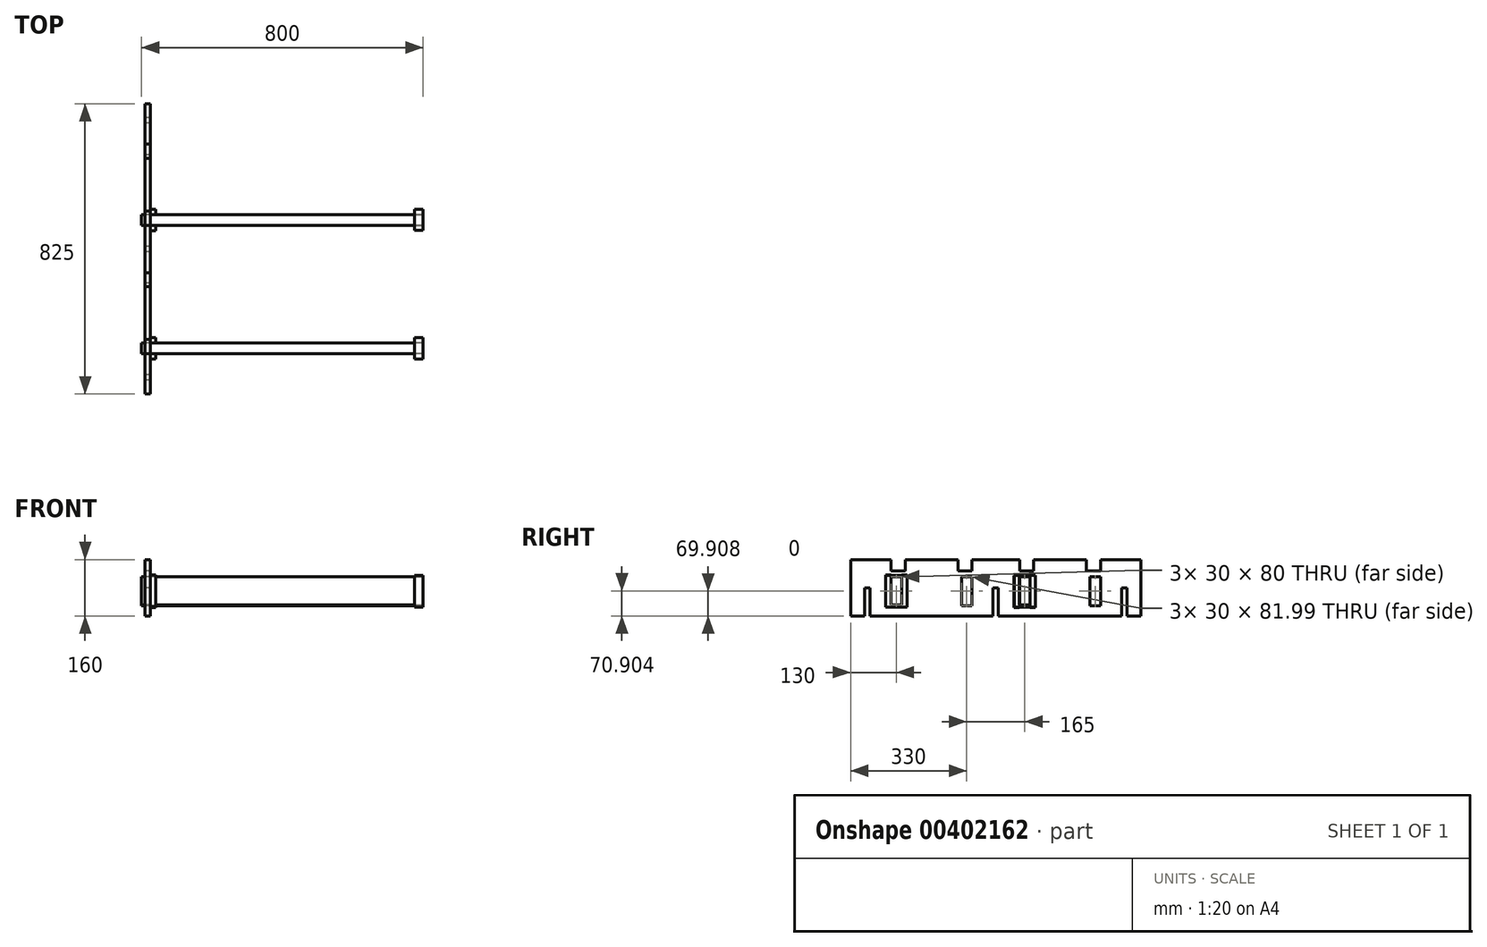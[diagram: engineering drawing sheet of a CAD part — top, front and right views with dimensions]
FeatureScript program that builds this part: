
annotation { "Feature Type Name" : "Feature", "Feature Type Description" : "" }
export const myFeature = defineFeature(function(context is Context, id is Id, definition is map)
    precondition{}
    {
        {
            var Q0;
            Q0=qCreatedBy(makeId("Right.planeOp"),FACE);
            var sketch = newSketch(context, id + "F0", { "sketchPlane" : qUnion([Q0])});
            skLineSegment(sketch, "E0.bottom", {"start": v(-412.5, 80) * mm, "end": v(-297.5, 80) * mm});
            skLineSegment(sketch, "E0.top", {"start": v(-412.5, -80) * mm, "end": v(-372.5, -80) * mm});
            skLineSegment(sketch, "E0.left", {"start": v(-412.5, 80) * mm, "end": v(-412.5, -80) * mm});
            skLineSegment(sketch, "E0.right", {"start": v(412.5, 80) * mm, "end": v(412.5, -80) * mm});
            skLineSegment(sketch, "E1", {"start": v(-372.5, -80) * mm, "end": v(-372.5, 0) * mm});
            skLineSegment(sketch, "E2", {"start": v(-372.5, 0) * mm, "end": v(-357.5, 0) * mm});
            skLineSegment(sketch, "E3", {"start": v(-357.5, 0) * mm, "end": v(-357.5, -80) * mm});
            skLineSegment(sketch, "E4", {"start": v(-7.5, -80) * mm, "end": v(-7.5, 0) * mm});
            skLineSegment(sketch, "E5", {"start": v(-7.5, 0) * mm, "end": v(7.5, 0) * mm});
            skLineSegment(sketch, "E6", {"start": v(7.5, 0) * mm, "end": v(7.5, -80) * mm});
            skLineSegment(sketch, "E7", {"start": v(357.5, -80) * mm, "end": v(357.5, 0) * mm});
            skLineSegment(sketch, "E8", {"start": v(357.5, 0) * mm, "end": v(372.5, 0) * mm});
            skLineSegment(sketch, "E9", {"start": v(372.5, 0) * mm, "end": v(372.5, -80) * mm});
            skLineSegment(sketch, "E10.trimOffspring", {"start": v(372.5, -80) * mm, "end": v(412.5, -80) * mm});
            skLineSegment(sketch, "E11", {"start": v(-357.5, -80) * mm, "end": v(-7.5, -80) * mm});
            skLineSegment(sketch, "E12", {"start": v(7.5, -80) * mm, "end": v(357.5, -80) * mm});
            skLineSegment(sketch, "E13", {"start": v(-297.5, 80) * mm, "end": v(-297.5, 48) * mm});
            skLineSegment(sketch, "E14", {"start": v(-297.5, 48) * mm, "end": v(-257.5, 48) * mm});
            skLineSegment(sketch, "E15", {"start": v(-257.5, 48) * mm, "end": v(-257.5, 80) * mm});
            skLineSegment(sketch, "E16", {"start": v(-257.5, 80) * mm, "end": v(-107.5, 80) * mm});
            skLineSegment(sketch, "E17", {"start": v(-107.5, 80) * mm, "end": v(-107.5, 48) * mm});
            skLineSegment(sketch, "E18", {"start": v(-107.5, 48) * mm, "end": v(-67.5, 48) * mm});
            skLineSegment(sketch, "E19", {"start": v(-67.5, 48) * mm, "end": v(-67.5, 80) * mm});
            skLineSegment(sketch, "E20", {"start": v(-67.5, 80) * mm, "end": v(67.5, 80) * mm});
            skLineSegment(sketch, "E21", {"start": v(67.5, 80) * mm, "end": v(67.5, 48) * mm});
            skLineSegment(sketch, "E22", {"start": v(67.5, 48) * mm, "end": v(107.5, 48) * mm});
            skLineSegment(sketch, "E23", {"start": v(107.5, 48) * mm, "end": v(107.5, 80) * mm});
            skLineSegment(sketch, "E24", {"start": v(107.5, 80) * mm, "end": v(257.5, 80) * mm});
            skLineSegment(sketch, "E25", {"start": v(257.5, 80) * mm, "end": v(257.5, 48) * mm});
            skLineSegment(sketch, "E26", {"start": v(257.5, 48) * mm, "end": v(297.5, 48) * mm});
            skLineSegment(sketch, "E27", {"start": v(297.5, 48) * mm, "end": v(297.5, 80) * mm});
            skLineSegment(sketch, "E28.trimOffspring", {"start": v(297.5, 80) * mm, "end": v(412.5, 80) * mm});
            skLineSegment(sketch, "E29.bottom", {"start": v(-297.5, 30.9) * mm, "end": v(-267.5, 30.9) * mm});
            skLineSegment(sketch, "E29.top", {"start": v(-297.5, -49.1) * mm, "end": v(-267.5, -49.1) * mm});
            skLineSegment(sketch, "E29.left", {"start": v(-297.5, 30.9) * mm, "end": v(-297.5, -49.1) * mm});
            skLineSegment(sketch, "E29.right", {"start": v(-267.5, 30.9) * mm, "end": v(-267.5, -49.1) * mm});
            skLineSegment(sketch, "E30.bottom", {"start": v(-67.5, 30.9) * mm, "end": v(-97.5, 30.9) * mm});
            skLineSegment(sketch, "E30.top", {"start": v(-67.5, -51.09) * mm, "end": v(-97.5, -51.09) * mm});
            skLineSegment(sketch, "E30.left", {"start": v(-67.5, 30.9) * mm, "end": v(-67.5, -51.09) * mm});
            skLineSegment(sketch, "E30.right", {"start": v(-97.5, 30.9) * mm, "end": v(-97.5, -51.09) * mm});
            skLineSegment(sketch, "E31.bottom", {"start": v(67.5, 30.9) * mm, "end": v(97.5, 30.9) * mm});
            skLineSegment(sketch, "E31.top", {"start": v(67.5, -51.09) * mm, "end": v(97.5, -51.09) * mm});
            skLineSegment(sketch, "E31.left", {"start": v(67.5, 30.9) * mm, "end": v(67.5, -51.09) * mm});
            skLineSegment(sketch, "E31.right", {"start": v(97.5, 30.9) * mm, "end": v(97.5, -51.09) * mm});
            skLineSegment(sketch, "E32.bottom", {"start": v(297.5, 30.9) * mm, "end": v(267.5, 30.9) * mm});
            skLineSegment(sketch, "E32.top", {"start": v(297.5, -51.09) * mm, "end": v(267.5, -51.09) * mm});
            skLineSegment(sketch, "E32.left", {"start": v(297.5, 30.9) * mm, "end": v(297.5, -51.09) * mm});
            skLineSegment(sketch, "E32.right", {"start": v(267.5, 30.9) * mm, "end": v(267.5, -51.09) * mm});
            skLineSegment(sketch, "E33", {"start": v(-357.5, -80) * mm, "end": v(-332.5, -80) * mm});
            skLineSegment(sketch, "E34", {"start": v(357.5, -80) * mm, "end": v(332.5, -80) * mm});
            skSolve(sketch);
        }
        {
            var Q0;
            Q0=qSketchRegion(id+"F0",true);
            extrude(context, id + "F1", {"entities" : qUnion([Q0]), "depth" : 15 * mm});
        }
        {
            var Q0;
            Q0=makeQuery(id+"F1.opExtrude","CAP_FACE",FACE,{"disambiguationData":[OSD([sQuery(id+"F0.wireOp",EDGE,"E0.bottom"),sQuery(id+"F0.wireOp",EDGE,"E0.top"),sQuery(id+"F0.wireOp",EDGE,"E0.left"),sQuery(id+"F0.wireOp",EDGE,"E0.right"),sQuery(id+"F0.wireOp",EDGE,"E1"),sQuery(id+"F0.wireOp",EDGE,"E2"),sQuery(id+"F0.wireOp",EDGE,"E3"),sQuery(id+"F0.wireOp",EDGE,"E4"),sQuery(id+"F0.wireOp",EDGE,"E5"),sQuery(id+"F0.wireOp",EDGE,"E6"),sQuery(id+"F0.wireOp",EDGE,"E7"),sQuery(id+"F0.wireOp",EDGE,"E8"),sQuery(id+"F0.wireOp",EDGE,"E9"),sQuery(id+"F0.wireOp",EDGE,"E10.trimOffspring"),sQuery(id+"F0.wireOp",EDGE,"E11"),sQuery(id+"F0.wireOp",EDGE,"E12"),sQuery(id+"F0.wireOp",EDGE,"E13"),sQuery(id+"F0.wireOp",EDGE,"E14"),sQuery(id+"F0.wireOp",EDGE,"E15"),sQuery(id+"F0.wireOp",EDGE,"E17"),sQuery(id+"F0.wireOp",EDGE,"E18"),sQuery(id+"F0.wireOp",EDGE,"E19"),sQuery(id+"F0.wireOp",EDGE,"E21"),sQuery(id+"F0.wireOp",EDGE,"E22"),sQuery(id+"F0.wireOp",EDGE,"E23"),sQuery(id+"F0.wireOp",EDGE,"E25"),sQuery(id+"F0.wireOp",EDGE,"E26"),sQuery(id+"F0.wireOp",EDGE,"E27"),sQuery(id+"F0.wireOp",EDGE,"E16"),sQuery(id+"F0.wireOp",EDGE,"E20"),sQuery(id+"F0.wireOp",EDGE,"E24"),sQuery(id+"F0.wireOp",EDGE,"E28.trimOffspring"),sQuery(id+"F0.wireOp",EDGE,"E29.bottom"),sQuery(id+"F0.wireOp",EDGE,"E29.top"),sQuery(id+"F0.wireOp",EDGE,"E29.left"),sQuery(id+"F0.wireOp",EDGE,"E29.right"),sQuery(id+"F0.wireOp",EDGE,"E30.bottom"),sQuery(id+"F0.wireOp",EDGE,"E30.top"),sQuery(id+"F0.wireOp",EDGE,"E30.left"),sQuery(id+"F0.wireOp",EDGE,"E30.right"),sQuery(id+"F0.wireOp",EDGE,"E31.bottom"),sQuery(id+"F0.wireOp",EDGE,"E31.top"),sQuery(id+"F0.wireOp",EDGE,"E31.left"),sQuery(id+"F0.wireOp",EDGE,"E31.right"),sQuery(id+"F0.wireOp",EDGE,"E32.bottom"),sQuery(id+"F0.wireOp",EDGE,"E32.top"),sQuery(id+"F0.wireOp",EDGE,"E32.left"),sQuery(id+"F0.wireOp",EDGE,"E32.right"),sQuery(id+"F0.wireOp",EDGE,"E33"),sQuery(id+"F0.wireOp",EDGE,"E34")])],"isStart":false});
            var sketch = newSketch(context, id + "F2", { "sketchPlane" : qUnion([Q0])});
            skLineSegment(sketch, "E35.bottom", {"start": v(-297.5, 35.68) * mm, "end": v(-312.5, 35.68) * mm});
            skLineSegment(sketch, "E35.top", {"start": v(-297.5, -54.32) * mm, "end": v(-312.5, -54.32) * mm});
            skLineSegment(sketch, "E35.left", {"start": v(-297.5, 35.68) * mm, "end": v(-297.5, -54.32) * mm});
            skLineSegment(sketch, "E35.right", {"start": v(-312.5, 35.68) * mm, "end": v(-312.5, -54.32) * mm});
            skLineSegment(sketch, "E36.bottom", {"start": v(-251.91, 36.37) * mm, "end": v(-266.91, 36.37) * mm});
            skLineSegment(sketch, "E36.top", {"start": v(-251.91, -53.63) * mm, "end": v(-266.91, -53.63) * mm});
            skLineSegment(sketch, "E36.left", {"start": v(-251.91, 36.37) * mm, "end": v(-251.91, -53.63) * mm});
            skLineSegment(sketch, "E36.right", {"start": v(-266.91, 36.37) * mm, "end": v(-266.91, -53.63) * mm});
            skLineSegment(sketch, "E37.bottom", {"start": v(67.21, 33.72) * mm, "end": v(52.21, 33.72) * mm});
            skLineSegment(sketch, "E37.top", {"start": v(67.21, -56.28) * mm, "end": v(52.21, -56.28) * mm});
            skLineSegment(sketch, "E37.left", {"start": v(67.21, 33.72) * mm, "end": v(67.21, -56.28) * mm});
            skLineSegment(sketch, "E37.right", {"start": v(52.21, 33.72) * mm, "end": v(52.21, -56.28) * mm});
            skLineSegment(sketch, "E38.bottom", {"start": v(112.33, 33.72) * mm, "end": v(97.33, 33.72) * mm});
            skLineSegment(sketch, "E38.top", {"start": v(112.33, -56.28) * mm, "end": v(97.33, -56.28) * mm});
            skLineSegment(sketch, "E38.left", {"start": v(112.33, 33.72) * mm, "end": v(112.33, -56.28) * mm});
            skLineSegment(sketch, "E38.right", {"start": v(97.33, 33.72) * mm, "end": v(97.33, -56.28) * mm});
            skSolve(sketch);
        }
        {
            var Q0;
            {var subQ2=sQuery(id+"F2.wireOp",EDGE,"E35.bottom");Q0=makeQuery(id+"F2.imprint","IMPRINT",FACE,{"disambiguationData":[TD([[makeQuery(id+"F2.imprint","IMPRINT",EDGE,{"derivedFrom":subQ2}),1.0]])]});}
            var Q1;
            Q1=makeQuery(id+"F2.imprint","IMPRINT",FACE,{"disambiguationData":[TD([[makeQuery(id+"F2.imprint","IMPRINT",EDGE,{"derivedFrom":sQuery(id+"F2.wireOp",EDGE,"E36.bottom")}),1.0]])]});
            var Q2;
            Q2=makeQuery(id+"F2.imprint","IMPRINT",FACE,{"disambiguationData":[TD([[makeQuery(id+"F2.imprint","IMPRINT",EDGE,{"derivedFrom":sQuery(id+"F2.wireOp",EDGE,"E37.bottom")}),1.0]])]});
            var Q3;
            {var subQ1=sQuery(id+"F2.wireOp",EDGE,"E38.bottom");Q3=makeQuery(id+"F2.imprint","IMPRINT",FACE,{"disambiguationData":[TD([[makeQuery(id+"F2.imprint","IMPRINT",EDGE,{"derivedFrom":subQ1}),1.0]])]});}
            extrude(context, id + "F3", {"entities" : qUnion([Q0, Q1, Q2, Q3]), "depth" : 15 * mm});
        }
        {
            var Q0;
            Q0=makeQuery(id+"F1.opExtrude","CAP_FACE",FACE,{"disambiguationData":[OSD([sQuery(id+"F0.wireOp",EDGE,"E0.bottom"),sQuery(id+"F0.wireOp",EDGE,"E0.top"),sQuery(id+"F0.wireOp",EDGE,"E0.left"),sQuery(id+"F0.wireOp",EDGE,"E0.right"),sQuery(id+"F0.wireOp",EDGE,"E1"),sQuery(id+"F0.wireOp",EDGE,"E2"),sQuery(id+"F0.wireOp",EDGE,"E3"),sQuery(id+"F0.wireOp",EDGE,"E4"),sQuery(id+"F0.wireOp",EDGE,"E5"),sQuery(id+"F0.wireOp",EDGE,"E6"),sQuery(id+"F0.wireOp",EDGE,"E7"),sQuery(id+"F0.wireOp",EDGE,"E8"),sQuery(id+"F0.wireOp",EDGE,"E9"),sQuery(id+"F0.wireOp",EDGE,"E10.trimOffspring"),sQuery(id+"F0.wireOp",EDGE,"E11"),sQuery(id+"F0.wireOp",EDGE,"E12"),sQuery(id+"F0.wireOp",EDGE,"E13"),sQuery(id+"F0.wireOp",EDGE,"E14"),sQuery(id+"F0.wireOp",EDGE,"E15"),sQuery(id+"F0.wireOp",EDGE,"E17"),sQuery(id+"F0.wireOp",EDGE,"E18"),sQuery(id+"F0.wireOp",EDGE,"E19"),sQuery(id+"F0.wireOp",EDGE,"E21"),sQuery(id+"F0.wireOp",EDGE,"E22"),sQuery(id+"F0.wireOp",EDGE,"E23"),sQuery(id+"F0.wireOp",EDGE,"E25"),sQuery(id+"F0.wireOp",EDGE,"E26"),sQuery(id+"F0.wireOp",EDGE,"E27"),sQuery(id+"F0.wireOp",EDGE,"E16"),sQuery(id+"F0.wireOp",EDGE,"E20"),sQuery(id+"F0.wireOp",EDGE,"E24"),sQuery(id+"F0.wireOp",EDGE,"E28.trimOffspring"),sQuery(id+"F0.wireOp",EDGE,"E29.bottom"),sQuery(id+"F0.wireOp",EDGE,"E29.top"),sQuery(id+"F0.wireOp",EDGE,"E29.left"),sQuery(id+"F0.wireOp",EDGE,"E29.right"),sQuery(id+"F0.wireOp",EDGE,"E30.bottom"),sQuery(id+"F0.wireOp",EDGE,"E30.top"),sQuery(id+"F0.wireOp",EDGE,"E30.left"),sQuery(id+"F0.wireOp",EDGE,"E30.right"),sQuery(id+"F0.wireOp",EDGE,"E31.bottom"),sQuery(id+"F0.wireOp",EDGE,"E31.top"),sQuery(id+"F0.wireOp",EDGE,"E31.left"),sQuery(id+"F0.wireOp",EDGE,"E31.right"),sQuery(id+"F0.wireOp",EDGE,"E32.bottom"),sQuery(id+"F0.wireOp",EDGE,"E32.top"),sQuery(id+"F0.wireOp",EDGE,"E32.left"),sQuery(id+"F0.wireOp",EDGE,"E32.right"),sQuery(id+"F0.wireOp",EDGE,"E33"),sQuery(id+"F0.wireOp",EDGE,"E34")])],"isStart":false});
            var sketch = newSketch(context, id + "F4", { "sketchPlane" : qUnion([Q0])});
            skLineSegment(sketch, "E39.bottom", {"start": v(-297.5, 30.9) * mm, "end": v(-267.5, 30.9) * mm});
            skLineSegment(sketch, "E39.top", {"start": v(-297.5, -49.1) * mm, "end": v(-267.5, -49.1) * mm});
            skLineSegment(sketch, "E39.left", {"start": v(-297.5, 30.9) * mm, "end": v(-297.5, -49.1) * mm});
            skLineSegment(sketch, "E39.right", {"start": v(-267.5, 30.9) * mm, "end": v(-267.5, -49.1) * mm});
            skLineSegment(sketch, "E40.bottom", {"start": v(67.5, 30.9) * mm, "end": v(97.5, 30.9) * mm});
            skLineSegment(sketch, "E40.top", {"start": v(67.5, -51.09) * mm, "end": v(97.5, -51.09) * mm});
            skLineSegment(sketch, "E40.left", {"start": v(67.5, 30.9) * mm, "end": v(67.5, -51.09) * mm});
            skLineSegment(sketch, "E40.right", {"start": v(97.5, 30.9) * mm, "end": v(97.5, -51.09) * mm});
            skSolve(sketch);
        }
        {
            var Q0;
            Q0=makeQuery(id+"F4.imprint","IMPRINT",FACE,{"disambiguationData":[TD([[makeQuery(id+"F4.imprint","IMPRINT",EDGE,{"derivedFrom":sQuery(id+"F4.wireOp",EDGE,"E40.bottom")}),-1.0]])]});
            var Q1;
            Q1=makeQuery(id+"F4.imprint","IMPRINT",FACE,{"disambiguationData":[TD([[makeQuery(id+"F4.imprint","IMPRINT",EDGE,{"derivedFrom":sQuery(id+"F4.wireOp",EDGE,"E39.bottom")}),-1.0]])]});
            extrude(context, id + "F5", {"entities" : qUnion([Q0, Q1]), "depth" : 775 * mm, "hasSecondDirection" : true, "secondDirectionOppositeDirection" : true, "secondDirectionDepth" : 25 * mm});
        }
        {
            var Q0;
            Q0=makeQuery(id+"F5.opExtrude","CAP_FACE",FACE,{"disambiguationData":[OSD([sQuery(id+"F4.wireOp",EDGE,"E39.bottom"),sQuery(id+"F4.wireOp",EDGE,"E39.top"),sQuery(id+"F4.wireOp",EDGE,"E39.left"),sQuery(id+"F4.wireOp",EDGE,"E39.right")])],"isStart":false});
            var sketch = newSketch(context, id + "F6", { "sketchPlane" : qUnion([Q0])});
            skLineSegment(sketch, "E41.bottom", {"start": v(-312.28, 34.58) * mm, "end": v(-252.28, 34.58) * mm});
            skLineSegment(sketch, "E41.top", {"start": v(-312.28, -55.42) * mm, "end": v(-252.28, -55.42) * mm});
            skLineSegment(sketch, "E41.left", {"start": v(-312.28, 34.58) * mm, "end": v(-312.28, -55.42) * mm});
            skLineSegment(sketch, "E41.right", {"start": v(-252.28, 34.58) * mm, "end": v(-252.28, -55.42) * mm});
            skLineSegment(sketch, "E42.bottom", {"start": v(-297.5, 30.9) * mm, "end": v(-267.5, 30.9) * mm});
            skLineSegment(sketch, "E42.top", {"start": v(-297.5, -49.1) * mm, "end": v(-267.5, -49.1) * mm});
            skLineSegment(sketch, "E42.left", {"start": v(-297.5, 30.9) * mm, "end": v(-297.5, -49.1) * mm});
            skLineSegment(sketch, "E42.right", {"start": v(-267.5, 30.9) * mm, "end": v(-267.5, -49.1) * mm});
            skLineSegment(sketch, "E43.bottom", {"start": v(53.21, 34.58) * mm, "end": v(113.21, 34.58) * mm});
            skLineSegment(sketch, "E43.top", {"start": v(53.21, -55.42) * mm, "end": v(113.21, -55.42) * mm});
            skLineSegment(sketch, "E43.left", {"start": v(53.21, 34.58) * mm, "end": v(53.21, -55.42) * mm});
            skLineSegment(sketch, "E43.right", {"start": v(113.21, 34.58) * mm, "end": v(113.21, -55.42) * mm});
            skLineSegment(sketch, "E44.bottom", {"start": v(67.15, 30.9) * mm, "end": v(97.15, 30.9) * mm});
            skLineSegment(sketch, "E44.top", {"start": v(67.15, -49.1) * mm, "end": v(97.15, -49.1) * mm});
            skLineSegment(sketch, "E44.left", {"start": v(67.15, 30.9) * mm, "end": v(67.15, -49.1) * mm});
            skLineSegment(sketch, "E44.right", {"start": v(97.15, 30.9) * mm, "end": v(97.15, -49.1) * mm});
            skSolve(sketch);
        }
        {
            var Q0;
            Q0 = qSketchRegion(id + "F6", true);
            extrude(context, id + "F7", {"entities" : qUnion([Q0]), "oppositeDirection" : true, "depth" : 25 * mm});
        }
    });
